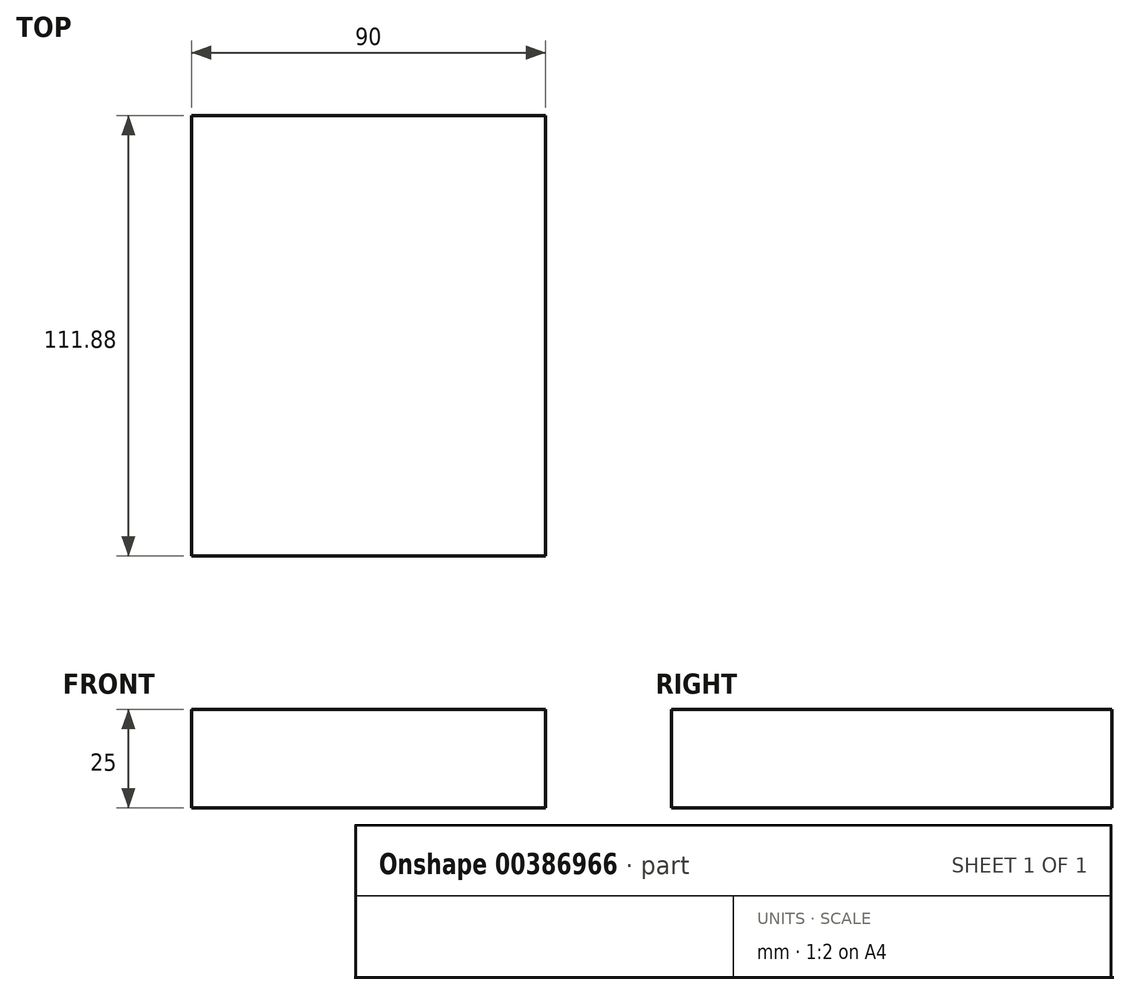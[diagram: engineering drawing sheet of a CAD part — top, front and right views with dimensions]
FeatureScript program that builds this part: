
annotation { "Feature Type Name" : "Feature", "Feature Type Description" : "" }
export const myFeature = defineFeature(function(context is Context, id is Id, definition is map)
    precondition{}
    {
        {
            var Q0;
            Q0=qCreatedBy(makeId("Top.planeOp"),FACE);
            var sketch = newSketch(context, id + "F0", { "sketchPlane" : qUnion([Q0])});
            skLineSegment(sketch, "E0.bottom", {"start": v(-45, 55.94) * mm, "end": v(45, 55.94) * mm});
            skLineSegment(sketch, "E0.top", {"start": v(-45, -55.94) * mm, "end": v(45, -55.94) * mm});
            skLineSegment(sketch, "E0.left", {"start": v(-45, 55.94) * mm, "end": v(-45, -55.94) * mm});
            skLineSegment(sketch, "E0.right", {"start": v(45, 55.94) * mm, "end": v(45, -55.94) * mm});
            skSolve(sketch);
        }
        {
            var Q0;
            Q0=makeQuery(id+"F0.imprint","IMPRINT",FACE,{"disambiguationData":[TD([[makeQuery(id+"F0.imprint","IMPRINT",EDGE,{"derivedFrom":sQuery(id+"F0.wireOp",EDGE,"E0.bottom")}),-1.0]])]});
            extrude(context, id + "F1", {"entities" : qUnion([Q0]), "endBound" : BoundingType.SYMMETRIC, "depth" : 25 * mm});
        }
    });
